# Revit family: AFBV-C_Roof_Exhauster
name_source: partatom
category: Mechanical Equipment
units: mm (PartAtom-declared; Revit-internal decimal feet)

## family parameters
Always vertical = Yes
Cut with Voids When Loaded = No
Part Type = Normal
Room Calculation Point = No
Round Connector Dimension = Use Diameter
Shared = No
Work Plane-Based = No

## types (11) — shared parameters
0 = 0' - 0"
1" = 0' - 1"
1.5 = 0' - 1 1/2"
2" = 0' - 2"
2' = 2' - 0"
3" = 0' - 3"
30 = 30.00°
4" = 0' - 4"
45 = 45.00°
60 = 60.00°
CENTER = 0' - 0"
Manufacturer = Loren Cook Company
Model = AFBV-C
ONE EIGTH = 0' - 0 1/8"
Type Comments = Tube Axial Fan Roof Exhauster Belt Drive Arrangement 9
URL = www.lorencook.com

## per-type parameters (varying)
- 12_AFBV-C_ROOF_EXHAUSTER: (A+.25")/2=0' - 6 9/16"; (E-.25")/2=0' - 10 7/8"; (H-(A/2))/2=0' - 9 3/32"; (J+(J-A))/2=0' - 10 11/32"; (J-A-.25")=0' - 4 15/16"; (K/2)-((J-A-.25")/2)=-0' - 2 9/32"; (L-1")/2=0' - 5 7/8"; (T_SQ+.125")/2=0' - 11 1/8"; -(E-.25")/2=-0' - 10 7/8"; -E/2=-0' - 11"; A=1' - 0 7/8"; A/2=0' - 6 7/16"; A/3=0' - 5 5/32"; B=1' - 3 5/8"; B/2=0' - 7 13/16"; B/2*1.1=0' - 8 19/32"; C=1' - 2 5/8"; C/2=0' - 7 5/16"; C/2+J=0' - 7 5/16"; E=1' - 10"; E-2"=1' - 8"; E/2=0' - 11"; F=0' - 0 5/16"; F/2=0' - 0 5/32"; G=6' - 0"; H=2' - 0 5/8"; H+J=2' - 0 5/8"; H-(A/2)=1' - 6 3/16"; J=1' - 6 1/16"; J/2=0' - 9 1/32"; K=0' - 0 3/8"; K/2=0' - 0 3/16"; L=1' - 0 3/4"; L/2=0' - 6 3/8"; RO=1' - 5 1/2"; RO/2=0' - 8 3/4"; T_SQ=1' - 10"; UP_A=3' - 0"; UP_A-E-3"=0' - 11"; UP_A_PLUS_VANE=3' - 6"; VANE=0' - 6"
- 16_AFBV-C_ROOF_EXHAUSTER: (A+.25")/2=0' - 8 9/16"; (E-.25")/2=1' - 0 3/8"; (H-(A/2))/2=0' - 10 27/32"; (J+(J-A))/2=1' - 0 11/32"; (J-A-.25")=0' - 4 15/16"; (K/2)-((J-A-.25")/2)=-0' - 2 9/32"; (L-1")/2=0' - 7 5/16"; (T_SQ+.125")/2=1' - 1 1/8"; -(E-.25")/2=-1' - 0 3/8"; -E/2=-1' - 0 1/2"; A=1' - 4 7/8"; A/2=0' - 8 7/16"; A/3=0' - 6 3/4"; B=1' - 7 5/8"; B/2=0' - 9 13/16"; B/2*1.1=0' - 10 25/32"; C=1' - 6 5/8"; C/2=0' - 9 5/16"; C/2+J=0' - 9 5/16"; E=2' - 1"; E-2"=1' - 11"; E/2=1' - 0 1/2"; F=0' - 0 5/16"; F/2=0' - 0 5/32"; G=6' - 0"; H=2' - 6 1/8"; H+J=2' - 6 1/8"; H-(A/2)=1' - 9 11/16"; J=1' - 10 1/16"; J/2=0' - 11 1/32"; K=0' - 0 3/8"; K/2=0' - 0 3/16"; L=1' - 3 5/8"; L/2=0' - 7 13/16"; RO=1' - 9 1/2"; RO/2=0' - 10 3/4"; T_SQ=2' - 2"; UP_A=3' - 3"; UP_A-E-3"=0' - 11"; UP_A_PLUS_VANE=4' - 1"; VANE=0' - 10"
- 18_AFBV-C_ROOF_EXHAUSTER: (A+.25")/2=0' - 9 9/16"; (E-.25")/2=1' - 0 3/8"; (H-(A/2))/2=0' - 10 27/32"; (J+(J-A))/2=1' - 1 11/32"; (J-A-.25")=0' - 4 15/16"; (K/2)-((J-A-.25")/2)=-0' - 2 9/32"; (L-1")/2=0' - 8"; (T_SQ+.125")/2=1' - 2 1/8"; -(E-.25")/2=-1' - 0 3/8"; -E/2=-1' - 0 1/2"; A=1' - 6 7/8"; A/2=0' - 9 7/16"; A/3=0' - 7 9/16"; B=1' - 9 5/8"; B/2=0' - 10 13/16"; B/2*1.1=0' - 11 29/32"; C=1' - 8 5/8"; C/2=0' - 10 5/16"; C/2+J=0' - 10 5/16"; E=2' - 1"; E-2"=1' - 11"; E/2=1' - 0 1/2"; F=0' - 0 5/16"; F/2=0' - 0 5/32"; G=6' - 0"; H=2' - 7 1/8"; H+J=2' - 7 1/8"; H-(A/2)=1' - 9 11/16"; J=2' - 0 1/16"; J/2=1' - 0 1/32"; K=0' - 0 3/8"; K/2=0' - 0 3/16"; L=1' - 5"; L/2=0' - 8 1/2"; RO=1' - 11 1/2"; RO/2=0' - 11 3/4"; T_SQ=2' - 4"; UP_A=3' - 11"; UP_A-E-3"=1' - 7"; UP_A_PLUS_VANE=4' - 10"; VANE=0' - 11"
- 24_AFBV-C_ROOF_EXHAUSTER: (A+.25")/2=1' - 0 9/16"; (E-.25")/2=1' - 3 3/8"; (H-(A/2))/2=1' - 1 23/32"; (J+(J-A))/2=1' - 4 29/32"; (J-A-.25")=0' - 5 11/16"; (K/2)-((J-A-.25")/2)=-0' - 2 21/32"; (L-1")/2=0' - 10 3/8"; (T_SQ+.125")/2=1' - 6 1/8"; -(E-.25")/2=-1' - 3 3/8"; -E/2=-1' - 3 1/2"; A=2' - 0 7/8"; A/2=1' - 0 7/16"; A/3=0' - 9 15/16"; B=2' - 5 1/8"; B/2=1' - 2 9/16"; B/2*1.1=1' - 4 1/32"; C=2' - 2 7/8"; C/2=1' - 1 7/16"; C/2+J=1' - 1 7/16"; E=2' - 7"; E-2"=2' - 5"; E/2=1' - 3 1/2"; F=0' - 0 7/16"; F/2=0' - 0 7/32"; G=6' - 0"; H=3' - 3 7/8"; H+J=3' - 3 7/8"; H-(A/2)=2' - 3 7/16"; J=2' - 6 13/16"; J/2=1' - 3 13/32"; K=0' - 0 3/8"; K/2=0' - 0 3/16"; L=1' - 9 3/4"; L/2=0' - 10 7/8"; RO=2' - 7 1/2"; RO/2=1' - 3 3/4"; T_SQ=3' - 0"; UP_A=4' - 6"; UP_A-E-3"=1' - 8"; UP_A_PLUS_VANE=5' - 7"; VANE=1' - 1"
- 28_AFBV-C_ROOF_EXHAUSTER: (A+.25")/2=1' - 2 9/16"; (E-.25")/2=1' - 3 3/8"; (H-(A/2))/2=1' - 1 23/32"; (J+(J-A))/2=1' - 6 29/32"; (J-A-.25")=0' - 5 11/16"; (K/2)-((J-A-.25")/2)=-0' - 2 21/32"; (L-1")/2=0' - 11 13/16"; (T_SQ+.125")/2=1' - 9 1/8"; -(E-.25")/2=-1' - 3 3/8"; -E/2=-1' - 3 1/2"; A=2' - 4 7/8"; A/2=1' - 2 7/16"; A/3=0' - 11 9/16"; B=2' - 9 1/8"; B/2=1' - 4 9/16"; B/2*1.1=1' - 6 7/32"; C=2' - 6 7/8"; C/2=1' - 3 7/16"; C/2+J=1' - 3 7/16"; E=2' - 7"; E-2"=2' - 5"; E/2=1' - 3 1/2"; F=0' - 0 7/16"; F/2=0' - 0 7/32"; G=6' - 0"; H=3' - 5 7/8"; H+J=3' - 5 7/8"; H-(A/2)=2' - 3 7/16"; J=2' - 10 13/16"; J/2=1' - 5 13/32"; K=0' - 0 3/8"; K/2=0' - 0 3/16"; L=2' - 0 5/8"; L/2=1' - 0 5/16"; RO=3' - 1 1/2"; RO/2=1' - 6 3/4"; T_SQ=3' - 6"; UP_A=4' - 6"; UP_A-E-3"=1' - 8"; UP_A_PLUS_VANE=5' - 7"; VANE=1' - 1"
- 32_AFBV-C_ROOF_EXHAUSTER: (A+.25")/2=1' - 4 5/8"; (E-.25")/2=1' - 4 7/8"; (H-(A/2))/2=1' - 2 3/8"; (J+(J-A))/2=1' - 9 23/32"; (J-A-.25")=0' - 6 11/16"; (K/2)-((J-A-.25")/2)=-0' - 3 1/8"; (L-1")/2=1' - 1 5/8"; (T_SQ+.125")/2=1' - 9 1/8"; -(E-.25")/2=-1' - 4 7/8"; -E/2=-1' - 5"; A=2' - 9"; A/2=1' - 4 1/2"; A/3=1' - 1 3/16"; B=3' - 1 1/4"; B/2=1' - 6 5/8"; B/2*1.1=1' - 8 1/2"; C=2' - 11"; C/2=1' - 5 1/2"; C/2+J=1' - 5 1/2"; E=2' - 10"; E-2"=2' - 8"; E/2=1' - 5"; F=0' - 0 7/16"; F/2=0' - 0 7/32"; G=6' - 0"; H=3' - 9 1/4"; H+J=3' - 9 1/4"; H-(A/2)=2' - 4 3/4"; J=3' - 3 15/16"; J/2=1' - 7 31/32"; K=0' - 0 7/16"; K/2=0' - 0 7/32"; L=2' - 4 1/4"; L/2=1' - 2 1/8"; RO=3' - 1 1/2"; RO/2=1' - 6 3/4"; T_SQ=3' - 6"; UP_A=5' - 3"; UP_A-E-3"=2' - 2"; UP_A_PLUS_VANE=6' - 6"; VANE=1' - 3"
- 36_AFBV-C_ROOF_EXHAUSTER: (A+.25")/2=1' - 6 5/8"; (E-.25")/2=1' - 4 7/8"; (H-(A/2))/2=1' - 2 3/8"; (J+(J-A))/2=1' - 11 23/32"; (J-A-.25")=0' - 6 11/16"; (K/2)-((J-A-.25")/2)=-0' - 3 1/8"; (L-1")/2=1' - 3 1/32"; (T_SQ+.125")/2=2' - 0 1/8"; -(E-.25")/2=-1' - 4 7/8"; -E/2=-1' - 5"; A=3' - 1"; A/2=1' - 6 1/2"; A/3=1' - 2 13/16"; B=3' - 5 3/8"; B/2=1' - 8 11/16"; B/2*1.1=1' - 10 3/4"; C=3' - 3"; C/2=1' - 7 1/2"; C/2+J=1' - 7 1/2"; E=2' - 10"; E-2"=2' - 8"; E/2=1' - 5"; F=0' - 0 7/16"; F/2=0' - 0 7/32"; G=6' - 0"; H=3' - 11 1/4"; H+J=3' - 11 1/4"; H-(A/2)=2' - 4 3/4"; J=3' - 7 15/16"; J/2=1' - 9 31/32"; K=0' - 0 7/16"; K/2=0' - 0 7/32"; L=2' - 7 1/16"; L/2=1' - 3 17/32"; RO=3' - 7 1/2"; RO/2=1' - 9 3/4"; T_SQ=4' - 0"; UP_A=5' - 3"; UP_A-E-3"=2' - 2"; UP_A_PLUS_VANE=6' - 7"; VANE=1' - 4"
- 44_AFBV-C_ROOF_EXHAUSTER: (A+.25")/2=1' - 10 5/8"; (E-.25")/2=1' - 8 7/8"; (H-(A/2))/2=1' - 6 1/8"; (J+(J-A))/2=2' - 3 3/4"; (J-A-.25")=0' - 6 3/4"; (K/2)-((J-A-.25")/2)=-0' - 3 5/32"; (L-1")/2=1' - 5 7/8"; (T_SQ+.125")/2=2' - 3 1/8"; -(E-.25")/2=-1' - 8 7/8"; -E/2=-1' - 9"; A=3' - 9"; A/2=1' - 10 1/2"; A/3=1' - 6"; B=4' - 1 3/8"; B/2=2' - 0 11/16"; B/2*1.1=2' - 3 5/32"; C=3' - 11 1/2"; C/2=1' - 11 3/4"; C/2+J=1' - 11 3/4"; E=3' - 6"; E-2"=3' - 4"; E/2=1' - 9"; F=0' - 0 7/16"; F/2=0' - 0 7/32"; G=12' - 0"; H=4' - 10 3/4"; H+J=4' - 10 3/4"; H-(A/2)=3' - 0 1/4"; J=4' - 4"; J/2=2' - 2"; K=0' - 0 7/16"; K/2=0' - 0 7/32"; L=3' - 0 3/4"; L/2=1' - 6 3/8"; RO=4' - 1 1/2"; RO/2=2' - 0 3/4"; T_SQ=4' - 6"; UP_A=6' - 11"; UP_A-E-3"=3' - 2"; UP_A_PLUS_VANE=8' - 6"; VANE=1' - 7"
- 48_AFBV-C_ROOF_EXHAUSTER: (A+.25")/2=2' - 0 11/16"; (E-.25")/2=1' - 8 7/8"; (H-(A/2))/2=1' - 6 3/32"; (J+(J-A))/2=2' - 6 9/16"; (J-A-.25")=0' - 7 3/4"; (K/2)-((J-A-.25")/2)=-0' - 3 21/32"; (L-1")/2=1' - 7 11/16"; (T_SQ+.125")/2=2' - 5 1/4"; -(E-.25")/2=-1' - 8 7/8"; -E/2=-1' - 9"; A=4' - 1 1/8"; A/2=2' - 0 9/16"; A/3=1' - 7 21/32"; B=4' - 5 1/2"; B/2=2' - 2 3/4"; B/2*1.1=2' - 5 7/16"; C=4' - 3 5/8"; C/2=2' - 1 13/16"; C/2+J=2' - 1 13/16"; E=3' - 6"; E-2"=3' - 4"; E/2=1' - 9"; F=0' - 0 7/16"; F/2=0' - 0 7/32"; G=12' - 0"; H=5' - 0 3/4"; H+J=5' - 0 3/4"; H-(A/2)=3' - 0 3/16"; J=4' - 9 1/8"; J/2=2' - 4 9/16"; K=0' - 0 7/16"; K/2=0' - 0 7/32"; L=3' - 4 3/8"; L/2=1' - 8 3/16"; RO=4' - 5 3/4"; RO/2=2' - 2 7/8"; T_SQ=4' - 10 1/4"; UP_A=6' - 11 1/2"; UP_A-E-3"=3' - 2 1/2"; UP_A_PLUS_VANE=8' - 9 1/2"; VANE=1' - 10"
- 54_AFBV-C_ROOF_EXHAUSTER: (A+.25")/2=2' - 3 13/16"; (E-.25")/2=1' - 8 7/8"; (H-(A/2))/2=1' - 0 1/32"; (J+(J-A))/2=2' - 9 7/8"; (J-A-.25")=0' - 8"; (K/2)-((J-A-.25")/2)=-0' - 3 25/32"; (L-1")/2=1' - 10"; (T_SQ+.125")/2=2' - 8 1/4"; -(E-.25")/2=-1' - 8 7/8"; -E/2=-1' - 9"; A=4' - 7 3/8"; A/2=2' - 3 11/16"; A/3=1' - 10 5/32"; B=5' - 0 3/4"; B/2=2' - 6 3/8"; B/2*1.1=2' - 9 13/32"; C=4' - 9 5/8"; C/2=2' - 4 13/16"; C/2+J=2' - 4 13/16"; E=3' - 6"; E-2"=3' - 4"; E/2=1' - 9"; F=0' - 0 7/16"; F/2=0' - 0 7/32"; G=12' - 0"; H=4' - 3 3/4"; H+J=4' - 3 3/4"; H-(A/2)=2' - 0 1/16"; J=5' - 3 5/8"; J/2=2' - 7 13/16"; K=0' - 0 7/16"; K/2=0' - 0 7/32"; L=3' - 9"; L/2=1' - 10 1/2"; RO=4' - 11 3/4"; RO/2=2' - 5 7/8"; T_SQ=5' - 4 1/4"; UP_A=6' - 11 1/2"; UP_A-E-3"=3' - 2 1/2"; UP_A_PLUS_VANE=8' - 10 1/2"; VANE=1' - 11"
- 60_AFBV-C_ROOF_EXHAUSTER: (A+.25")/2=2' - 6 13/16"; (E-.25")/2=1' - 8 7/8"; (H-(A/2))/2=1' - 0 1/32"; (J+(J-A))/2=3' - 0 11/16"; (J-A-.25")=0' - 7 3/4"; (K/2)-((J-A-.25")/2)=-0' - 3 21/32"; (L-1")/2=2' - 0 1/32"; (T_SQ+.125")/2=2' - 11 1/4"; -(E-.25")/2=-1' - 8 7/8"; -E/2=-1' - 9"; A=5' - 1 3/8"; A/2=2' - 6 11/16"; A/3=2' - 0 9/16"; B=5' - 6 3/4"; B/2=2' - 9 3/8"; B/2*1.1=3' - 0 23/32"; C=5' - 3 5/8"; C/2=2' - 7 13/16"; C/2+J=2' - 7 13/16"; E=3' - 6"; E-2"=3' - 4"; E/2=1' - 9"; F=0' - 3"; F/2=0' - 1 1/2"; G=12' - 0"; H=4' - 6 3/4"; H+J=4' - 6 3/4"; H-(A/2)=2' - 0 1/16"; J=5' - 9 3/8"; J/2=2' - 10 11/16"; K=0' - 0 7/16"; K/2=0' - 0 7/32"; L=4' - 1 1/16"; L/2=2' - 0 17/32"; RO=5' - 5 3/4"; RO/2=2' - 8 7/8"; T_SQ=5' - 10 1/4"; UP_A=6' - 11 1/2"; UP_A-E-3"=3' - 2 1/2"; UP_A_PLUS_VANE=9' - 0 1/2"; VANE=2' - 1"

## geometry (parser evidence)
native form markers: Sweep x1
no freeform markers — native parametric forms only
